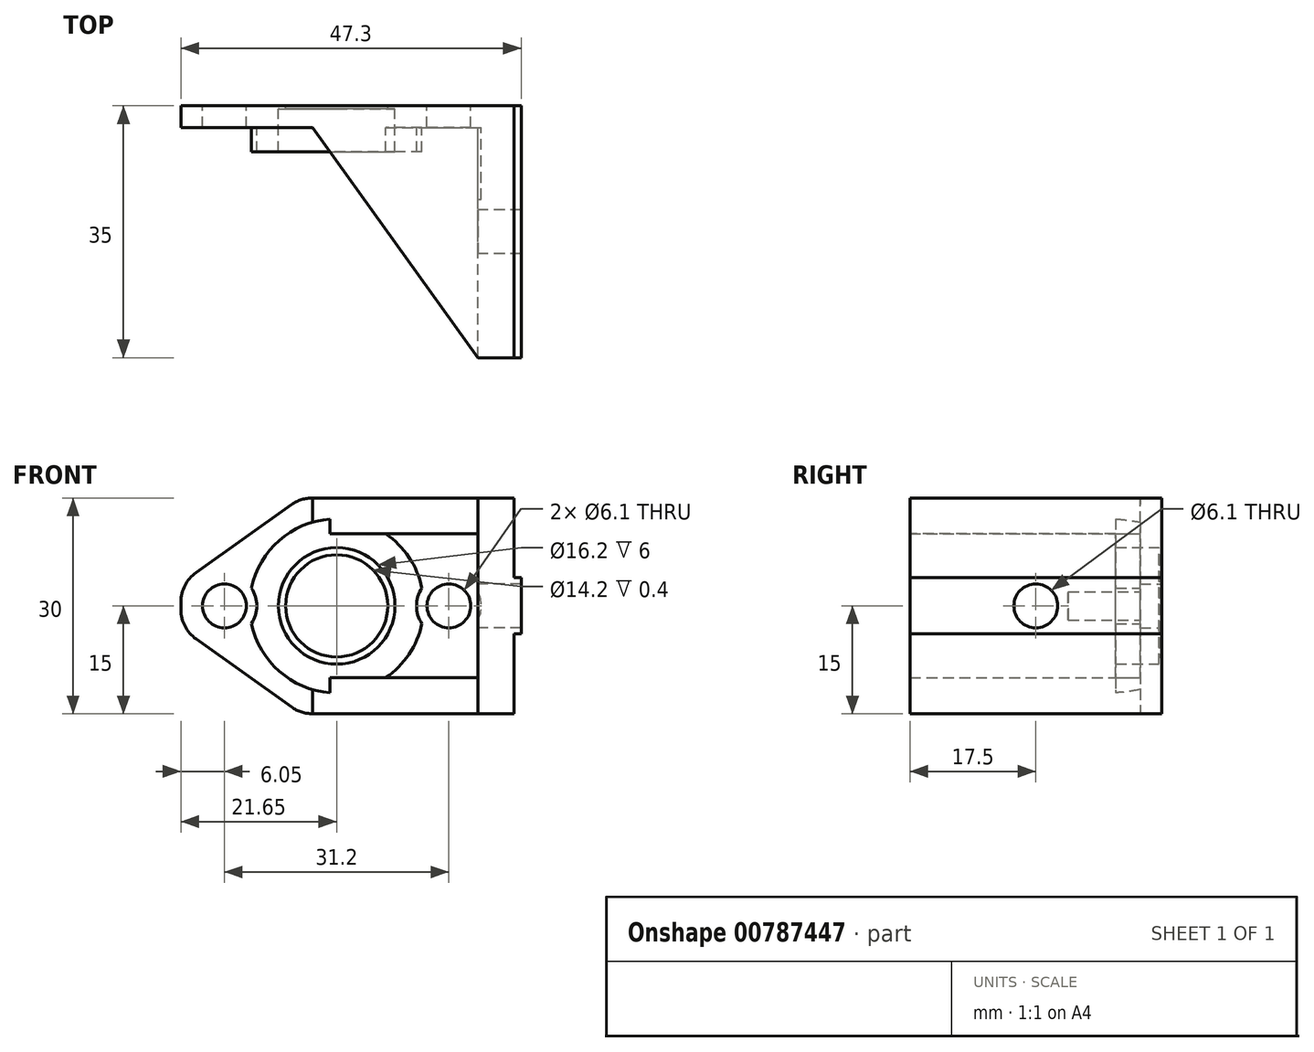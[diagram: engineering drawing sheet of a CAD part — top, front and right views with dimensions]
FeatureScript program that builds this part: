
annotation { "Feature Type Name" : "Feature", "Feature Type Description" : "" }
export const myFeature = defineFeature(function(context is Context, id is Id, definition is map)
    precondition{}
    {
        {
            var Q0;
            Q0=qCreatedBy(makeId("Front.planeOp"),FACE);
            var sketch = newSketch(context, id + "F0", { "sketchPlane" : qUnion([Q0])});
            skLineSegment(sketch, "E0.right", {"start": v(-21.65, -0.54) * mm, "end": v(-21.65, 0.54) * mm});
            skPoint(sketch, "E0.middle", {"position": v(0, 0) * mm});
            skCircle(sketch, "E1", {"center": v(-15.6, 0) * mm, "radius": 3.05 * mm});
            skCircle(sketch, "E2.MirrorC", {"center": v(15.6, 0) * mm, "radius": 3.05 * mm});
            skCircle(sketch, "E3", {"center": v(0, 0) * mm, "radius": 8.1 * mm});
            skCircle(sketch, "E4", {"center": v(0, 0) * mm, "radius": 12.1 * mm});
            skLineSegment(sketch, "E5", {"start": v(-17.37, 2.48) * mm, "end": v(-7.02, 9.86) * mm, "construction": true});
            skLineSegment(sketch, "E6", {"start": v(-19.55, 4.61) * mm, "end": v(-6.27, 14.07) * mm});
            skPoint(sketch, "E7.visualSharp", {"position": v(-21.65, 3.12) * mm});
            skArc(sketch, "E7.filletArc", {"start": v(-19.55, 4.61) * mm, "mid": v(-21.1, 2.83) * mm, "end": v(-21.65, 0.54) * mm});
            skArc(sketch, "E8.filletArc", {"start": v(-3.37, 15) * mm, "mid": v(-4.9, 14.76) * mm, "end": v(-6.27, 14.07) * mm});
            skArc(sketch, "E9.MirrorCS", {"start": v(-19.55, -4.61) * mm, "mid": v(-21.1, -2.83) * mm, "end": v(-21.65, -0.54) * mm});
            skLineSegment(sketch, "E10.MirrorCS", {"start": v(-19.55, -4.61) * mm, "end": v(-6.27, -14.07) * mm});
            skArc(sketch, "E11.MirrorCS", {"start": v(-3.37, -15) * mm, "mid": v(-4.9, -14.76) * mm, "end": v(-6.27, -14.07) * mm});
            skPoint(sketch, "E12.orphan", {"position": v(-21.65, -15) * mm});
            skLineSegment(sketch, "E13", {"start": v(-3.37, 15) * mm, "end": v(19.65, 15) * mm});
            skLineSegment(sketch, "E14", {"start": v(19.65, 15) * mm, "end": v(19.65, -15) * mm});
            skLineSegment(sketch, "E15", {"start": v(19.65, -15) * mm, "end": v(-3.37, -15) * mm});
            skLineSegment(sketch, "E16.bottom", {"start": v(19.65, 15) * mm, "end": v(24.65, 15) * mm});
            skLineSegment(sketch, "E16.top", {"start": v(19.65, -15) * mm, "end": v(24.65, -15) * mm});
            skLineSegment(sketch, "E16.right", {"start": v(24.65, 15) * mm, "end": v(24.65, -15) * mm});
            skSolve(sketch);
        }
        {
            var Q0;
            Q0=makeQuery(id+"F0.imprint","IMPRINT",FACE,{"disambiguationData":[TD([[makeQuery(id+"F0.imprint","IMPRINT",EDGE,{"derivedFrom":sQuery(id+"F0.wireOp",EDGE,"E3")}),-1.0]])]});
            extrude(context, id + "F1", {"entities" : qUnion([Q0]), "depth" : 6.4 * mm, "offsetDistance" : 25 * mm});
        }
        {
            var Q0;
            Q0 = qSketchRegion(id + "F0", true);
            extrude(context, id + "F2", {"entities" : qUnion([Q0]), "operationType" : NewBodyOperationType.ADD, "depth" : 3 * mm, "offsetDistance" : 25 * mm});
        }
        {
            var Q0;
            {var subQ0=sQuery(id+"F0.wireOp",EDGE,"E4");Q0=makeQuery(id+"F2.boolean.opBoolean","MERGE",FACE,{"derivedFrom":[makeQuery(id+"F1.opExtrude","CAP_FACE",FACE,{"disambiguationData":[OSD([sQuery(id+"F0.wireOp",EDGE,"E3"),subQ0])],"isStart":true}),makeQuery(id+"F2.opExtrude","CAP_FACE",FACE,{"disambiguationData":[OSD([sQuery(id+"F0.wireOp",EDGE,"E0.bottom"),sQuery(id+"F0.wireOp",EDGE,"E0.top"),sQuery(id+"F0.wireOp",EDGE,"E0.left"),sQuery(id+"F0.wireOp",EDGE,"E0.right"),sQuery(id+"F0.wireOp",EDGE,"E1"),sQuery(id+"F0.wireOp",EDGE,"E2.MirrorC"),subQ0,sQuery(id+"F0.wireOp",EDGE,"E6"),sQuery(id+"F0.wireOp",EDGE,"E7.filletArc"),sQuery(id+"F0.wireOp",EDGE,"E8.filletArc"),sQuery(id+"F0.wireOp",EDGE,"a1945099-096e-447e-bc1c-ab5cae43a46e0.MirrorCS"),sQuery(id+"F0.wireOp",EDGE,"e7613415-c0dd-44c2-a091-62de6971341e0.MirrorCS"),sQuery(id+"F0.wireOp",EDGE,"568613a7-9c33-49a0-9674-28169e1cce0e0.MirrorCS"),sQuery(id+"F0.wireOp",EDGE,"E9.MirrorCS"),sQuery(id+"F0.wireOp",EDGE,"E10.MirrorCS"),sQuery(id+"F0.wireOp",EDGE,"E11.MirrorCS"),sQuery(id+"F0.wireOp",EDGE,"7480bcef-4817-4377-8283-0c3d8621cf620.MirrorCS"),sQuery(id+"F0.wireOp",EDGE,"9ec5c487-3746-435e-b199-95de8daa40a20.MirrorCS"),sQuery(id+"F0.wireOp",EDGE,"8ba82cc5-7c4e-43a8-960a-3daafe53bb050.MirrorCS")])],"isStart":true})]});}
            var sketch = newSketch(context, id + "F3", { "sketchPlane" : qUnion([Q0])});
            skCircle(sketch, "E17", {"center": v(0, 0) * mm, "radius": 7.1 * mm});
            skSolve(sketch);
        }
        {
            var Q0;
            Q0=makeQuery(id+"F3.imprint","IMPRINT",FACE,{"disambiguationData":[TD([[makeQuery(id+"F3.imprint","IMPRINT",EDGE,{"derivedFrom":sQuery(id+"F3.wireOp",EDGE,"E17")}),-1.0]])]});
            extrude(context, id + "F4", {"entities" : qUnion([Q0]), "operationType" : NewBodyOperationType.ADD, "oppositeDirection" : true, "depth" : 0.4 * mm, "offsetDistance" : 25 * mm});
        }
        {
            var Q0;
            Q0=makeQuery(id+"F0.imprint","IMPRINT",FACE,{"disambiguationData":[TD([[makeQuery(id+"F0.imprint","IMPRINT",EDGE,{"derivedFrom":sQuery(id+"F0.wireOp",EDGE,"E16.bottom")}),-1.0]])]});
            extrude(context, id + "F5", {"entities" : qUnion([Q0]), "operationType" : NewBodyOperationType.ADD, "depth" : 35 * mm, "offsetDistance" : 25 * mm});
        }
        {
            var Q0;
            Q0=makeQuery(id+"F2.opExtrude","CAP_FACE",FACE,{"disambiguationData":[OSD([sQuery(id+"F0.wireOp",EDGE,"E0.right"),sQuery(id+"F0.wireOp",EDGE,"E1"),sQuery(id+"F0.wireOp",EDGE,"E2.MirrorC"),sQuery(id+"F0.wireOp",EDGE,"E4"),sQuery(id+"F0.wireOp",EDGE,"E6"),sQuery(id+"F0.wireOp",EDGE,"E7.filletArc"),sQuery(id+"F0.wireOp",EDGE,"E8.filletArc"),sQuery(id+"F0.wireOp",EDGE,"E9.MirrorCS"),sQuery(id+"F0.wireOp",EDGE,"E10.MirrorCS"),sQuery(id+"F0.wireOp",EDGE,"E11.MirrorCS"),sQuery(id+"F0.wireOp",EDGE,"E13"),sQuery(id+"F0.wireOp",EDGE,"E15"),sQuery(id+"F0.wireOp",EDGE,"E16.bottom"),sQuery(id+"F0.wireOp",EDGE,"E16.top"),sQuery(id+"F0.wireOp",EDGE,"E16.right")])],"isStart":false});
            var sketch = newSketch(context, id + "F6", { "sketchPlane" : qUnion([Q0])});
            skLineSegment(sketch, "E18", {"start": v(-0.37, 0) * mm, "end": v(28.02, 0) * mm, "construction": true});
            skLineSegment(sketch, "E19", {"start": v(15.6, 0) * mm, "end": v(15.6, -7.1) * mm, "construction": true});
            skLineSegment(sketch, "E20", {"start": v(0, 0) * mm, "end": v(-25.26, 0) * mm, "construction": true});
            skLineSegment(sketch, "E21", {"start": v(-15.6, 0) * mm, "end": v(-15.6, -7.65) * mm, "construction": true});
            skCircle(sketch, "E22", {"center": v(-15.6, 0) * mm, "radius": 4.5 * mm});
            skCircle(sketch, "E23", {"center": v(15.6, 0) * mm, "radius": 4.5 * mm});
            skSolve(sketch);
        }
        {
            var Q0;
            Q0 = qSketchRegion(id + "F6", true);
            extrude(context, id + "F7", {"entities" : qUnion([Q0]), "operationType" : NewBodyOperationType.REMOVE, "depth" : 10 * mm, "offsetDistance" : 25 * mm});
        }
        {
            var Q0;
            {var subQ0=sQuery(id+"F0.wireOp",EDGE,"E16.top");Q0=makeQuery(id+"F5.boolean.opBoolean","MERGE",FACE,{"derivedFrom":[makeQuery(id+"F2.opExtrude","SWEPT_FACE",FACE,{"disambiguationData":[OSD([sQuery(id+"F0.wireOp",EDGE,"E15"),subQ0])]}),makeQuery(id+"F5.opExtrude","SWEPT_FACE",FACE,{"disambiguationData":[OSD([subQ0])]})]});}
            var sketch = newSketch(context, id + "F8", { "sketchPlane" : qUnion([Q0])});
            skLineSegment(sketch, "E24", {"start": v(19.65, 35) * mm, "end": v(-3.37, 3) * mm});
            skLineSegment(sketch, "E25", {"start": v(-3.37, 3) * mm, "end": v(19.65, 3) * mm});
            skLineSegment(sketch, "E26", {"start": v(19.65, 3) * mm, "end": v(19.65, 35) * mm});
            skSolve(sketch);
        }
        {
            var Q0;
            Q0=makeQuery(id+"F8.imprint","IMPRINT",FACE,{"disambiguationData":[TD([[makeQuery(id+"F8.imprint","IMPRINT",EDGE,{"derivedFrom":sQuery(id+"F8.wireOp",EDGE,"E24")}),1.0]])]});
            extrude(context, id + "F9", {"entities" : qUnion([Q0]), "operationType" : NewBodyOperationType.ADD, "oppositeDirection" : true, "depth" : 5 * mm, "offsetDistance" : 25 * mm});
        }
        {
            var Q0;
            {var subQ0=sQuery(id+"F0.wireOp",EDGE,"E16.bottom");Q0=makeQuery(id+"F5.boolean.opBoolean","MERGE",FACE,{"derivedFrom":[makeQuery(id+"F2.opExtrude","SWEPT_FACE",FACE,{"disambiguationData":[OSD([sQuery(id+"F0.wireOp",EDGE,"E13"),subQ0])]}),makeQuery(id+"F5.opExtrude","SWEPT_FACE",FACE,{"disambiguationData":[OSD([subQ0])]})]});}
            var sketch = newSketch(context, id + "F10", { "sketchPlane" : qUnion([Q0])});
            skLineSegment(sketch, "E27", {"start": v(-3.37, -3) * mm, "end": v(19.65, -35) * mm});
            skLineSegment(sketch, "E28", {"start": v(19.65, -35) * mm, "end": v(19.65, -3) * mm});
            skLineSegment(sketch, "E29", {"start": v(19.65, -3) * mm, "end": v(-3.37, -3) * mm});
            skSolve(sketch);
        }
        {
            var Q0;
            Q0=makeQuery(id+"F10.imprint","IMPRINT",FACE,{"disambiguationData":[TD([[makeQuery(id+"F10.imprint","IMPRINT",EDGE,{"derivedFrom":sQuery(id+"F10.wireOp",EDGE,"E27")}),1.0]])]});
            extrude(context, id + "F11", {"entities" : qUnion([Q0]), "operationType" : NewBodyOperationType.ADD, "oppositeDirection" : true, "depth" : 5 * mm, "offsetDistance" : 25 * mm});
        }
        {
            var Q0;
            {var subQ0=sQuery(id+"F0.wireOp",EDGE,"E16.right");Q0=makeQuery(id+"F5.boolean.opBoolean","MERGE",FACE,{"derivedFrom":[makeQuery(id+"F2.opExtrude","SWEPT_FACE",FACE,{"disambiguationData":[OSD([subQ0])]}),makeQuery(id+"F5.opExtrude","SWEPT_FACE",FACE,{"disambiguationData":[OSD([subQ0])]})]});}
            var sketch = newSketch(context, id + "F12", { "sketchPlane" : qUnion([Q0])});
            skLineSegment(sketch, "E30", {"start": v(0, 0) * mm, "end": v(-35, 0) * mm, "construction": true});
            skLineSegment(sketch, "E31.bottom", {"start": v(0, 3.9) * mm, "end": v(-35, 3.9) * mm});
            skLineSegment(sketch, "E31.top", {"start": v(0, -3.9) * mm, "end": v(-35, -3.9) * mm});
            skLineSegment(sketch, "E31.left", {"start": v(0, 3.9) * mm, "end": v(0, -3.9) * mm});
            skLineSegment(sketch, "E31.right", {"start": v(-35, 3.9) * mm, "end": v(-35, -3.9) * mm});
            skPoint(sketch, "E31.middle", {"position": v(-17.5, 0) * mm});
            skCircle(sketch, "E32", {"center": v(-17.5, 0) * mm, "radius": 3.05 * mm});
            skSolve(sketch);
        }
        {
            var Q0;
            Q0=makeQuery(id+"F12.imprint","IMPRINT",FACE,{"disambiguationData":[TD([[makeQuery(id+"F12.imprint","IMPRINT",EDGE,{"derivedFrom":sQuery(id+"F12.wireOp",EDGE,"E31.bottom")}),1.0]])]});
            extrude(context, id + "F13", {"entities" : qUnion([Q0]), "operationType" : NewBodyOperationType.ADD, "depth" : 1 * mm, "offsetDistance" : 25 * mm});
        }
        {
            var Q0;
            {var subQ0=sQuery(id+"F0.wireOp",EDGE,"E16.right");Q0=makeQuery(id+"F13.boolean.opBoolean","SPLIT",FACE,{"disambiguationData":[TD([makeQuery(id+"F13.opExtrude","SWEPT_FACE",FACE,{"disambiguationData":[OSD([sQuery(id+"F12.wireOp",EDGE,"E32")])]})])],"derivedFrom":makeQuery(id+"F5.boolean.opBoolean","MERGE",FACE,{"derivedFrom":[makeQuery(id+"F2.opExtrude","SWEPT_FACE",FACE,{"disambiguationData":[OSD([subQ0])]}),makeQuery(id+"F5.opExtrude","SWEPT_FACE",FACE,{"disambiguationData":[OSD([subQ0])]})]})});}
            extrude(context, id + "F14", {"entities" : qUnion([Q0]), "operationType" : NewBodyOperationType.REMOVE, "endBound" : BoundingType.THROUGH_ALL, "oppositeDirection" : true, "depth" : 25 * mm, "offsetDistance" : 25 * mm});
        }
    });
